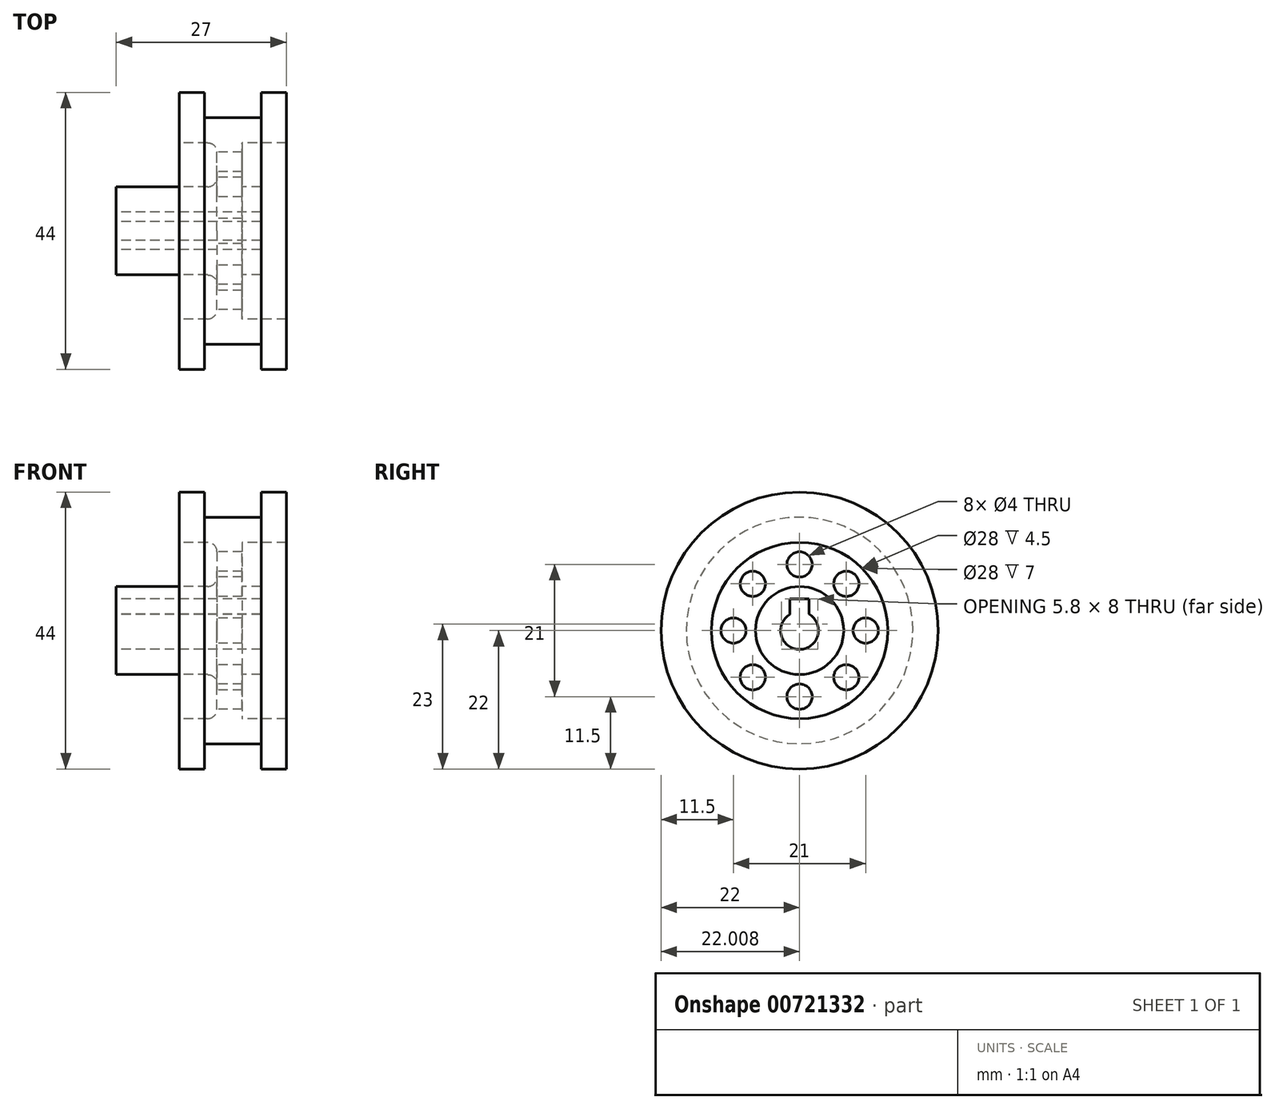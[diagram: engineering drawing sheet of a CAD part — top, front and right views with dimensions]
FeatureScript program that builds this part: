
annotation { "Feature Type Name" : "Feature", "Feature Type Description" : "" }
export const myFeature = defineFeature(function(context is Context, id is Id, definition is map)
    precondition{}
    {
        {
            var Q0;
            Q0=qCreatedBy(makeId("Front.planeOp"),FACE);
            var sketch = newSketch(context, id + "F0", { "sketchPlane" : qUnion([Q0])});
            skLineSegment(sketch, "E0", {"start": v(-14.09, -3) * mm, "end": v(8.91, -3) * mm});
            skLineSegment(sketch, "E1", {"start": v(-14.09, -3) * mm, "end": v(-14.09, -7) * mm});
            skLineSegment(sketch, "E2", {"start": v(-14.09, -7) * mm, "end": v(1.91, -7) * mm});
            skLineSegment(sketch, "E3", {"start": v(1.91, -7) * mm, "end": v(1.91, -14) * mm});
            skLineSegment(sketch, "E4", {"start": v(1.91, -14) * mm, "end": v(-4.09, -14) * mm});
            skLineSegment(sketch, "E5", {"start": v(-4.09, -14) * mm, "end": v(-4.09, -22) * mm});
            skLineSegment(sketch, "E6", {"start": v(-4.09, -22) * mm, "end": v(-0.09, -22) * mm});
            skLineSegment(sketch, "E7", {"start": v(-0.09, -22) * mm, "end": v(-0.09, -18) * mm});
            skLineSegment(sketch, "E8", {"start": v(-0.09, -18) * mm, "end": v(8.91, -18) * mm});
            skLineSegment(sketch, "E9", {"start": v(8.91, -18) * mm, "end": v(8.91, -22) * mm});
            skLineSegment(sketch, "E10", {"start": v(8.91, -22) * mm, "end": v(12.91, -22) * mm});
            skLineSegment(sketch, "E11", {"start": v(12.91, -22) * mm, "end": v(12.91, -14) * mm});
            skLineSegment(sketch, "E12", {"start": v(12.91, -14) * mm, "end": v(5.91, -14) * mm});
            skLineSegment(sketch, "E13", {"start": v(5.91, -14) * mm, "end": v(5.91, -7) * mm});
            skLineSegment(sketch, "E14", {"start": v(5.91, -7) * mm, "end": v(8.91, -7) * mm});
            skLineSegment(sketch, "E15", {"start": v(8.91, -7) * mm, "end": v(8.91, -3) * mm});
            skLineSegment(sketch, "E16", {"start": v(-20.75, 0) * mm, "end": v(18.13, 0) * mm, "construction": true});
            skSolve(sketch);
        }
        {
            var Q0;
            Q0=makeQuery(id+"F0.imprint","IMPRINT",FACE,{"disambiguationData":[TD([[makeQuery(id+"F0.imprint","IMPRINT",EDGE,{"derivedFrom":sQuery(id+"F0.wireOp",EDGE,"E0")}),-1.0]])]});
            var Q1;
            Q1=sQuery(id+"F0.wireOp",EDGE,"E16");
            revolve(context, id + "F1", {"surfaceOperationType" : NewSurfaceOperationType.NEW, "entities" : qUnion([Q0]), "axis" : qUnion([Q1]), "revolveType" : RevolveType.FULL});
        }
        {
            var Q0;
            Q0=makeQuery(id+"F1.opRevolve","SWEPT_FACE",FACE,{"disambiguationData":[OSD([sQuery(id+"F0.wireOp",EDGE,"E3")])]});
            fillet(context, id + "F2", {"entities" : qUnion([Q0]), "radius" : 1.5 * mm, "tangentPropagation" : true, "allowEdgeOverflow" : false});
        }
        {
            var Q0;
            Q0=makeQuery(id+"F1.opRevolve","SWEPT_FACE",FACE,{"disambiguationData":[OSD([sQuery(id+"F0.wireOp",EDGE,"E3")])]});
            var sketch = newSketch(context, id + "F3", { "sketchPlane" : qUnion([Q0])});
            skCircle(sketch, "E17", {"center": v(-10.5, 0) * mm, "radius": 2 * mm});
            skCircle(sketch, "E18.1.0", {"center": v(-7.42, -7.42) * mm, "radius": 2 * mm});
            skCircle(sketch, "E18.2.0", {"center": v(0, -10.5) * mm, "radius": 2 * mm});
            skCircle(sketch, "E18.3.0", {"center": v(7.42, -7.42) * mm, "radius": 2 * mm});
            skCircle(sketch, "E18.4.0", {"center": v(10.5, 0) * mm, "radius": 2 * mm});
            skCircle(sketch, "E18.5.0", {"center": v(7.42, 7.42) * mm, "radius": 2 * mm});
            skCircle(sketch, "E18.6.0", {"center": v(0, 10.5) * mm, "radius": 2 * mm});
            skCircle(sketch, "E18.7.0", {"center": v(-7.42, 7.42) * mm, "radius": 2 * mm});
            skPoint(sketch, "E18.center", {"position": v(0, 0) * mm});
            skSolve(sketch);
        }
        {
            var Q0;
            Q0 = qSketchRegion(id + "F3", true);
            extrude(context, id + "F4", {"entities" : qUnion([Q0]), "operationType" : NewBodyOperationType.REMOVE, "oppositeDirection" : true, "depth" : 25 * mm, "offsetDistance" : 25 * mm});
        }
        {
            var Q0;
            Q0=makeQuery(id+"F1.opRevolve","SWEPT_FACE",FACE,{"disambiguationData":[OSD([sQuery(id+"F0.wireOp",EDGE,"E1")])]});
            var sketch = newSketch(context, id + "F5", { "sketchPlane" : qUnion([Q0])});
            skLineSegment(sketch, "E19.bottom", {"start": v(-1.47, 0) * mm, "end": v(1.53, 0) * mm});
            skLineSegment(sketch, "E19.top", {"start": v(-1.47, 5) * mm, "end": v(1.53, 5) * mm});
            skLineSegment(sketch, "E19.left", {"start": v(-1.47, 0) * mm, "end": v(-1.47, 5) * mm});
            skLineSegment(sketch, "E19.right", {"start": v(1.53, 0) * mm, "end": v(1.53, 5) * mm});
            skSolve(sketch);
        }
        {
            var Q0;
            Q0 = qSketchRegion(id + "F5", true);
            extrude(context, id + "F6", {"entities" : qUnion([Q0]), "operationType" : NewBodyOperationType.REMOVE, "oppositeDirection" : true, "depth" : 50 * mm, "offsetDistance" : 25 * mm});
        }
    });
